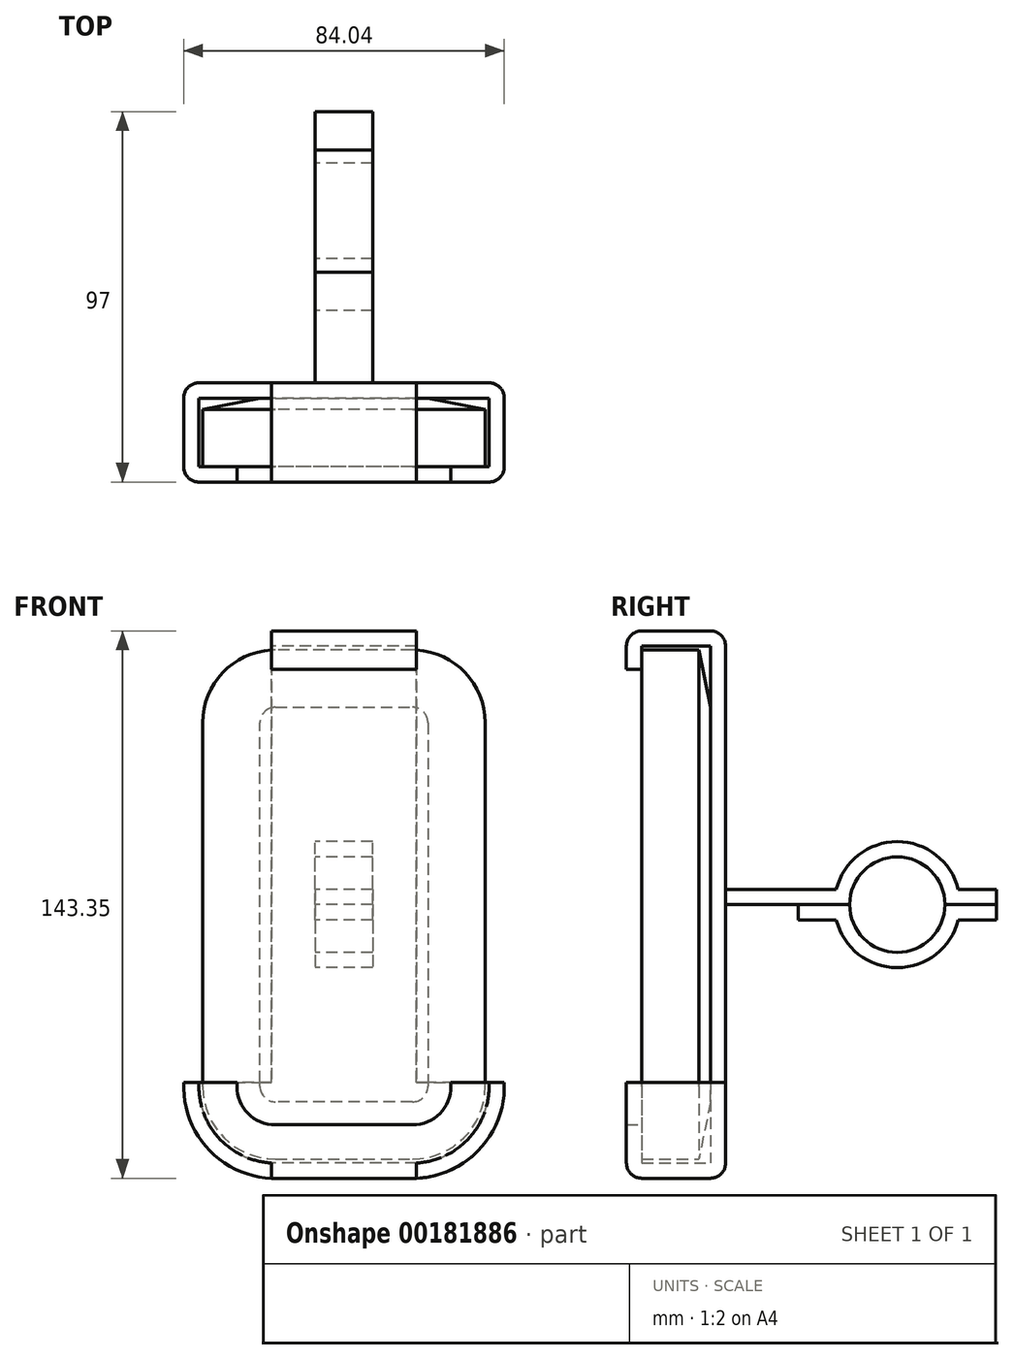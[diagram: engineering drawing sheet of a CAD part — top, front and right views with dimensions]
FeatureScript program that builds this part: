
annotation { "Feature Type Name" : "Feature", "Feature Type Description" : "" }
export const myFeature = defineFeature(function(context is Context, id is Id, definition is map)
    precondition{}
    {
        {
            var Q0;
            Q0=qCreatedBy(makeId("Front.planeOp"),FACE);
            var sketch = newSketch(context, id + "F0", { "sketchPlane" : qUnion([Q0])});
            skLineSegment(sketch, "E0.bottom", {"start": v(17.95, -66.68) * mm, "end": v(-17.95, -66.68) * mm});
            skLineSegment(sketch, "E0.top", {"start": v(17.95, 66.68) * mm, "end": v(-17.95, 66.68) * mm});
            skLineSegment(sketch, "E0.left", {"start": v(37, -47.63) * mm, "end": v(37, 47.63) * mm});
            skLineSegment(sketch, "E0.right", {"start": v(-37, -47.63) * mm, "end": v(-37, 47.63) * mm});
            skPoint(sketch, "E0.middle", {"position": v(0, 0) * mm});
            skPoint(sketch, "E1.visualSharp", {"position": v(-37, 66.68) * mm});
            skArc(sketch, "E1.filletArc", {"start": v(-17.95, 66.68) * mm, "mid": v(-31.42, 61.1) * mm, "end": v(-37, 47.63) * mm});
            skPoint(sketch, "E2.visualSharp", {"position": v(37, 66.68) * mm});
            skArc(sketch, "E2.filletArc", {"start": v(37, 47.63) * mm, "mid": v(31.42, 61.1) * mm, "end": v(17.95, 66.68) * mm});
            skPoint(sketch, "E3.visualSharp", {"position": v(37, -66.68) * mm});
            skArc(sketch, "E3.filletArc", {"start": v(17.95, -66.68) * mm, "mid": v(31.42, -61.1) * mm, "end": v(37, -47.63) * mm});
            skPoint(sketch, "E4.visualSharp", {"position": v(-37, -66.68) * mm});
            skArc(sketch, "E4.filletArc", {"start": v(-37, -47.63) * mm, "mid": v(-31.42, -61.1) * mm, "end": v(-17.95, -66.68) * mm});
            skSolve(sketch);
        }
        {
            var Q0;
            Q0 = qSketchRegion(id + "F0", true);
            extrude(context, id + "F1", {"entities" : qUnion([Q0]), "depth" : 18 * mm});
        }
        {
            var Q0;
            Q0=makeQuery(id+"F1.opExtrude","CAP_FACE",FACE,{"disambiguationData":[OSD([sQuery(id+"F0.wireOp",EDGE,"E0.bottom"),sQuery(id+"F0.wireOp",EDGE,"E0.top"),sQuery(id+"F0.wireOp",EDGE,"E0.left"),sQuery(id+"F0.wireOp",EDGE,"E0.right"),sQuery(id+"F0.wireOp",EDGE,"E1.filletArc"),sQuery(id+"F0.wireOp",EDGE,"E2.filletArc"),sQuery(id+"F0.wireOp",EDGE,"E3.filletArc"),sQuery(id+"F0.wireOp",EDGE,"E4.filletArc")])],"isStart":true});
            chamfer(context, id + "F2", {"entities" : qUnion([Q0]), "chamferType" : ChamferType.TWO_OFFSETS, "width1" : 15 * mm, "oppositeDirection" : false, "width2" : 3 * mm, "tangentPropagation" : true});
        }
        {
            var Q0;
            Q0=qCreatedBy(makeId("Right.planeOp"),FACE);
            var sketch = newSketch(context, id + "F3", { "sketchPlane" : qUnion([Q0])});
            skLineSegment(sketch, "E5", {"start": v(-18, 67.68) * mm, "end": v(-18, 61.68) * mm});
            skLineSegment(sketch, "E6", {"start": v(-18, 61.68) * mm, "end": v(-22, 61.68) * mm});
            skLineSegment(sketch, "E7", {"start": v(-22, 61.68) * mm, "end": v(-22, 67.68) * mm});
            skLineSegment(sketch, "E8", {"start": v(-18, 71.68) * mm, "end": v(0, 71.68) * mm});
            skLineSegment(sketch, "E9", {"start": v(4, 67.68) * mm, "end": v(4, -67.67) * mm});
            skLineSegment(sketch, "E10", {"start": v(0, -71.67) * mm, "end": v(-18, -71.67) * mm});
            skLineSegment(sketch, "E11", {"start": v(-22, -67.67) * mm, "end": v(-22, -57.67) * mm});
            skLineSegment(sketch, "E12", {"start": v(-22, -57.67) * mm, "end": v(-18, -57.67) * mm});
            skLineSegment(sketch, "E13", {"start": v(-18, -57.67) * mm, "end": v(-18, -67.67) * mm});
            skLineSegment(sketch, "E14", {"start": v(-18, -67.67) * mm, "end": v(0, -67.67) * mm});
            skLineSegment(sketch, "E15", {"start": v(0, -67.67) * mm, "end": v(0, 67.68) * mm});
            skLineSegment(sketch, "E16", {"start": v(0, 67.68) * mm, "end": v(-18, 67.68) * mm});
            skLineSegment(sketch, "E17", {"start": v(-1.45, 66.68) * mm, "end": v(-18, 66.68) * mm});
            skLineSegment(sketch, "E18.0", {"start": v(-1.45, 67.68) * mm, "end": v(-18, 67.68) * mm});
            skLineSegment(sketch, "E19", {"start": v(-18, 66.68) * mm, "end": v(-18, 67.68) * mm});
            skPoint(sketch, "E20.visualSharp", {"position": v(4, 71.68) * mm});
            skArc(sketch, "E20.filletArc", {"start": v(4, 67.68) * mm, "mid": v(2.83, 70.5) * mm, "end": v(0, 71.68) * mm});
            skPoint(sketch, "E21.visualSharp", {"position": v(-22, 71.68) * mm});
            skArc(sketch, "E21.filletArc", {"start": v(-18, 71.68) * mm, "mid": v(-20.83, 70.5) * mm, "end": v(-22, 67.68) * mm});
            skPoint(sketch, "E22.visualSharp", {"position": v(4, -71.67) * mm});
            skArc(sketch, "E22.filletArc", {"start": v(0, -71.67) * mm, "mid": v(2.83, -70.5) * mm, "end": v(4, -67.67) * mm});
            skPoint(sketch, "E23.visualSharp", {"position": v(-22, -71.67) * mm});
            skArc(sketch, "E23.filletArc", {"start": v(-22, -67.67) * mm, "mid": v(-20.83, -70.5) * mm, "end": v(-18, -71.67) * mm});
            skSolve(sketch);
        }
        {
            var Q0;
            Q0 = qSketchRegion(id + "F3", true);
            extrude(context, id + "F4", {"entities" : qUnion([Q0]), "endBound" : BoundingType.SYMMETRIC, "depth" : 38 * mm});
        }
        {
            var Q0;
            Q0=makeQuery(id+"F4.opExtrude","CAP_FACE",FACE,{"disambiguationData":[OSD([sQuery(id+"F3.wireOp",EDGE,"E5"),sQuery(id+"F3.wireOp",EDGE,"E6"),sQuery(id+"F3.wireOp",EDGE,"E7"),sQuery(id+"F3.wireOp",EDGE,"E8"),sQuery(id+"F3.wireOp",EDGE,"E9"),sQuery(id+"F3.wireOp",EDGE,"E10"),sQuery(id+"F3.wireOp",EDGE,"E11"),sQuery(id+"F3.wireOp",EDGE,"E12"),sQuery(id+"F3.wireOp",EDGE,"E13"),sQuery(id+"F3.wireOp",EDGE,"E14"),sQuery(id+"F3.wireOp",EDGE,"E15"),sQuery(id+"F3.wireOp",EDGE,"E16"),sQuery(id+"F3.wireOp",EDGE,"E18.0"),sQuery(id+"F3.wireOp",EDGE,"E19"),sQuery(id+"F3.wireOp",EDGE,"E20.filletArc"),sQuery(id+"F3.wireOp",EDGE,"E21.filletArc"),sQuery(id+"F3.wireOp",EDGE,"E22.filletArc"),sQuery(id+"F3.wireOp",EDGE,"E23.filletArc")])],"isStart":false});
            var sketch = newSketch(context, id + "F5", { "sketchPlane" : qUnion([Q0])});
            skLineSegment(sketch, "E24", {"start": v(-18, -67.67) * mm, "end": v(-18, -57.67) * mm});
            skLineSegment(sketch, "E25", {"start": v(-18, -57.67) * mm, "end": v(-22, -57.67) * mm});
            skLineSegment(sketch, "E26", {"start": v(-22, -57.67) * mm, "end": v(-22, -67.67) * mm});
            skArc(sketch, "E27", {"start": v(-22, -67.67) * mm, "mid": v(-20.83, -70.5) * mm, "end": v(-18, -71.67) * mm});
            skLineSegment(sketch, "E28", {"start": v(-18, -71.67) * mm, "end": v(0, -71.67) * mm});
            skArc(sketch, "E29", {"start": v(0, -71.67) * mm, "mid": v(2.83, -70.5) * mm, "end": v(4, -67.67) * mm});
            skLineSegment(sketch, "E30", {"start": v(4, -67.67) * mm, "end": v(4, -57.67) * mm});
            skLineSegment(sketch, "E31", {"start": v(4, -57.67) * mm, "end": v(0, -57.67) * mm});
            skLineSegment(sketch, "E32", {"start": v(0, -57.67) * mm, "end": v(0, -67.67) * mm});
            skLineSegment(sketch, "E33", {"start": v(0, -67.67) * mm, "end": v(-18, -67.67) * mm});
            skLineSegment(sketch, "E34.bottom", {"start": v(0, -57.67) * mm, "end": v(4, -57.67) * mm});
            skLineSegment(sketch, "E34.top", {"start": v(0, -47.17) * mm, "end": v(4, -47.17) * mm});
            skLineSegment(sketch, "E34.left", {"start": v(0, -57.67) * mm, "end": v(0, -47.17) * mm});
            skLineSegment(sketch, "E34.right", {"start": v(4, -57.67) * mm, "end": v(4, -47.17) * mm});
            skSolve(sketch);
        }
        {
            var Q0;
            Q0=qCreatedBy(makeId("Right.planeOp"),FACE);
            cPlane(context, id + "F6", {"entities" : qUnion([Q0]), "cplaneType" : CPlaneType.OFFSET, "offset" : 17.95 * mm, "width" : 150 * mm, "height" : 150 * mm});
        }
        {
            var Q0;
            Q0=qCreatedBy(id+"F6.planeOp",FACE);
            var sketch = newSketch(context, id + "F7", { "sketchPlane" : qUnion([Q0])});
            skLineSegment(sketch, "E35", {"start": v(0, -47.63) * mm, "end": v(-26.79, -47.63) * mm});
            skSolve(sketch);
        }
        {
            var Q0;
            Q0=makeQuery(id+"F5.imprint","IMPRINT",FACE,{"disambiguationData":[TD([[makeQuery(id+"F5.imprint","IMPRINT",EDGE,{"derivedFrom":sQuery(id+"F5.wireOp",EDGE,"E24")}),-1.0]])]});
            var Q1;
            Q1=sQuery(id+"F7.wireOp",EDGE,"E35");
            revolve(context, id + "F8", {"entities" : qUnion([Q0]), "axis" : qUnion([Q1]), "revolveType" : RevolveType.ONE_DIRECTION, "angle" : 90 * degree});
        }
        {
            var Q0;
            Q0=makeQuery(id+"F8.opRevolve","SWEPT_BODY",BODY,{"disambiguationData":[OSD([sQuery(id+"F5.wireOp",EDGE,"E24"),sQuery(id+"F5.wireOp",EDGE,"E25"),sQuery(id+"F5.wireOp",EDGE,"E26"),sQuery(id+"F5.wireOp",EDGE,"E27"),sQuery(id+"F5.wireOp",EDGE,"E28"),sQuery(id+"F5.wireOp",EDGE,"E29"),sQuery(id+"F5.wireOp",EDGE,"E30"),sQuery(id+"F5.wireOp",EDGE,"E31"),sQuery(id+"F5.wireOp",EDGE,"E32"),sQuery(id+"F5.wireOp",EDGE,"E33")])]});
            var Q1;
            Q1=qCreatedBy(makeId("Right.planeOp"),FACE);
            mirror(context, id + "F9", {"entities" : qUnion([Q0]), "mirrorPlane" : qUnion([Q1])});
        }
        {
            var Q0;
            Q0=makeQuery(id+"F9.opPattern","COPY",BODY,{"derivedFrom":makeQuery(id+"F8.opRevolve","SWEPT_BODY",BODY,{"disambiguationData":[OSD([sQuery(id+"F5.wireOp",EDGE,"E24"),sQuery(id+"F5.wireOp",EDGE,"E25"),sQuery(id+"F5.wireOp",EDGE,"E26"),sQuery(id+"F5.wireOp",EDGE,"E27"),sQuery(id+"F5.wireOp",EDGE,"E28"),sQuery(id+"F5.wireOp",EDGE,"E29"),sQuery(id+"F5.wireOp",EDGE,"E30"),sQuery(id+"F5.wireOp",EDGE,"E31"),sQuery(id+"F5.wireOp",EDGE,"E32"),sQuery(id+"F5.wireOp",EDGE,"E33")])]}),"instanceName":"1"});
            var Q1;
            Q1=makeQuery(id+"F8.opRevolve","SWEPT_BODY",BODY,{"disambiguationData":[OSD([sQuery(id+"F5.wireOp",EDGE,"E24"),sQuery(id+"F5.wireOp",EDGE,"E25"),sQuery(id+"F5.wireOp",EDGE,"E26"),sQuery(id+"F5.wireOp",EDGE,"E27"),sQuery(id+"F5.wireOp",EDGE,"E28"),sQuery(id+"F5.wireOp",EDGE,"E29"),sQuery(id+"F5.wireOp",EDGE,"E30"),sQuery(id+"F5.wireOp",EDGE,"E31"),sQuery(id+"F5.wireOp",EDGE,"E32"),sQuery(id+"F5.wireOp",EDGE,"E33")])]});
            var Q2;
            Q2=makeQuery(id+"F4.opExtrude","SWEPT_BODY",BODY,{"disambiguationData":[OSD([sQuery(id+"F3.wireOp",EDGE,"E5"),sQuery(id+"F3.wireOp",EDGE,"E6"),sQuery(id+"F3.wireOp",EDGE,"E7"),sQuery(id+"F3.wireOp",EDGE,"E8"),sQuery(id+"F3.wireOp",EDGE,"E9"),sQuery(id+"F3.wireOp",EDGE,"E10"),sQuery(id+"F3.wireOp",EDGE,"E11"),sQuery(id+"F3.wireOp",EDGE,"E12"),sQuery(id+"F3.wireOp",EDGE,"E13"),sQuery(id+"F3.wireOp",EDGE,"E14"),sQuery(id+"F3.wireOp",EDGE,"E15"),sQuery(id+"F3.wireOp",EDGE,"E16"),sQuery(id+"F3.wireOp",EDGE,"E18.0"),sQuery(id+"F3.wireOp",EDGE,"E19"),sQuery(id+"F3.wireOp",EDGE,"E20.filletArc"),sQuery(id+"F3.wireOp",EDGE,"E21.filletArc"),sQuery(id+"F3.wireOp",EDGE,"E22.filletArc"),sQuery(id+"F3.wireOp",EDGE,"E23.filletArc")])]});
            booleanBodies(context, id + "F10", {"operationType" : BooleanOperationType.UNION, "tools" : qUnion([Q0, Q1, Q2])});
        }
        {
            var Q0;
            {var subQ0=makeQuery(id+"F8.opRevolve","SWEPT_FACE",FACE,{"disambiguationData":[OSD([sQuery(id+"F5.wireOp",EDGE,"E30")])]});Q0=makeQuery(id+"F10.opBoolean","MERGE",FACE,{"derivedFrom":[makeQuery(id+"F4.opExtrude","SWEPT_FACE",FACE,{"disambiguationData":[OSD([sQuery(id+"F3.wireOp",EDGE,"E9")])]}),subQ0,makeQuery(id+"F9.opPattern","COPY",FACE,{"derivedFrom":subQ0,"instanceName":"1"})]});}
            var sketch = newSketch(context, id + "F11", { "sketchPlane" : qUnion([Q0])});
            skLineSegment(sketch, "E36", {"start": v(-28, -46.58) * mm, "end": v(-19, -46.58) * mm});
            skLineSegment(sketch, "E37", {"start": v(-19, -46.58) * mm, "end": v(-19, -57.67) * mm});
            skArc(sketch, "E38", {"start": v(-28, -46.58) * mm, "mid": v(-25.8, -53.99) * mm, "end": v(-19, -57.67) * mm});
            skLineSegment(sketch, "E39", {"start": v(0, 0) * mm, "end": v(0, -77.7) * mm});
            skPoint(sketch, "E39.endSnap0", {"position": v(0, -67.67) * mm});
            skLineSegment(sketch, "E40.MirrorCS", {"start": v(-19, -46.58) * mm, "end": v(-19, -35.48) * mm});
            skLineSegment(sketch, "E41.MirrorCS", {"start": v(19, -46.58) * mm, "end": v(19, -57.67) * mm});
            skLineSegment(sketch, "E42.MirrorCS", {"start": v(28, -46.58) * mm, "end": v(19, -46.58) * mm});
            skArc(sketch, "E43.MirrorCS", {"start": v(28, -46.58) * mm, "mid": v(25.8, -53.99) * mm, "end": v(19, -57.67) * mm});
            skSolve(sketch);
        }
        {
            var Q0;
            Q0 = qSketchRegion(id + "F11", true);
            extrude(context, id + "F12", {"entities" : qUnion([Q0]), "operationType" : NewBodyOperationType.ADD, "oppositeDirection" : true, "depth" : 4 * mm});
        }
        {
            var Q0;
            Q0=qCreatedBy(makeId("Right.planeOp"),FACE);
            var sketch = newSketch(context, id + "F13", { "sketchPlane" : qUnion([Q0])});
            skLineSegment(sketch, "E44", {"start": v(0, 0) * mm, "end": v(36.5, 0) * mm});
            skLineSegment(sketch, "E45", {"start": v(75, 0) * mm, "end": v(75, 4) * mm});
            skLineSegment(sketch, "E46", {"start": v(75, 4) * mm, "end": v(65, 4) * mm});
            skLineSegment(sketch, "E47", {"start": v(0, 4) * mm, "end": v(0, 0) * mm});
            skArc(sketch, "E48", {"start": v(61.5, 0) * mm, "mid": v(49, 12.5) * mm, "end": v(36.5, 0) * mm});
            skArc(sketch, "E49.0", {"start": v(65, 4) * mm, "mid": v(49, 16.5) * mm, "end": v(32.98, 4) * mm});
            skLineSegment(sketch, "E50.trimOffspring", {"start": v(32.98, 4) * mm, "end": v(0, 4) * mm});
            skLineSegment(sketch, "E51.trimOffspring", {"start": v(61.5, 0) * mm, "end": v(75, 0) * mm});
            skArc(sketch, "E52.MirrorCS", {"start": v(61.5, 0) * mm, "mid": v(49, -12.5) * mm, "end": v(36.5, 0) * mm});
            skArc(sketch, "E53.MirrorCS", {"start": v(65, -4) * mm, "mid": v(49, -16.5) * mm, "end": v(32.98, -4) * mm});
            skLineSegment(sketch, "E54.MirrorCS", {"start": v(75, -4) * mm, "end": v(65, -4) * mm});
            skLineSegment(sketch, "E55", {"start": v(49, 0) * mm, "end": v(49, -28.1) * mm});
            skPoint(sketch, "E55.endSnap0", {"position": v(49, -16.5) * mm});
            skLineSegment(sketch, "E56.MirrorCS", {"start": v(22.98, -4) * mm, "end": v(32.98, -4) * mm});
            skLineSegment(sketch, "E57", {"start": v(22.98, -4) * mm, "end": v(22.98, 0) * mm});
            skLineSegment(sketch, "E58", {"start": v(75, -4) * mm, "end": v(75, 0) * mm});
            skSolve(sketch);
        }
        {
            var Q0;
            Q0=makeQuery(id+"F13.imprint","IMPRINT",FACE,{"disambiguationData":[TD([[makeQuery(id+"F13.imprint","IMPRINT",EDGE,{"derivedFrom":sQuery(id+"F13.wireOp",EDGE,"E45")}),1.0]])]});
            extrude(context, id + "F14", {"entities" : qUnion([Q0]), "operationType" : NewBodyOperationType.ADD, "endBound" : BoundingType.SYMMETRIC, "depth" : 15 * mm});
        }
        {
            var Q0;
            {var subQ8=sQuery(id+"F13.wireOp",EDGE,"E56.MirrorCS");Q0=makeQuery(id+"F13.imprint","IMPRINT",FACE,{"disambiguationData":[TD([[makeQuery(id+"F13.imprint","IMPRINT",EDGE,{"derivedFrom":subQ8}),1.0]])]});}
            var Q1;
            {var subQ5=sQuery(id+"F13.wireOp",EDGE,"E51.trimOffspring");Q1=makeQuery(id+"F13.imprint","IMPRINT",FACE,{"disambiguationData":[TD([[makeQuery(id+"F13.imprint","IMPRINT",EDGE,{"derivedFrom":subQ5}),-1.0]])]});}
            extrude(context, id + "F15", {"entities" : qUnion([Q0, Q1]), "endBound" : BoundingType.SYMMETRIC, "depth" : 15 * mm});
        }
    });
